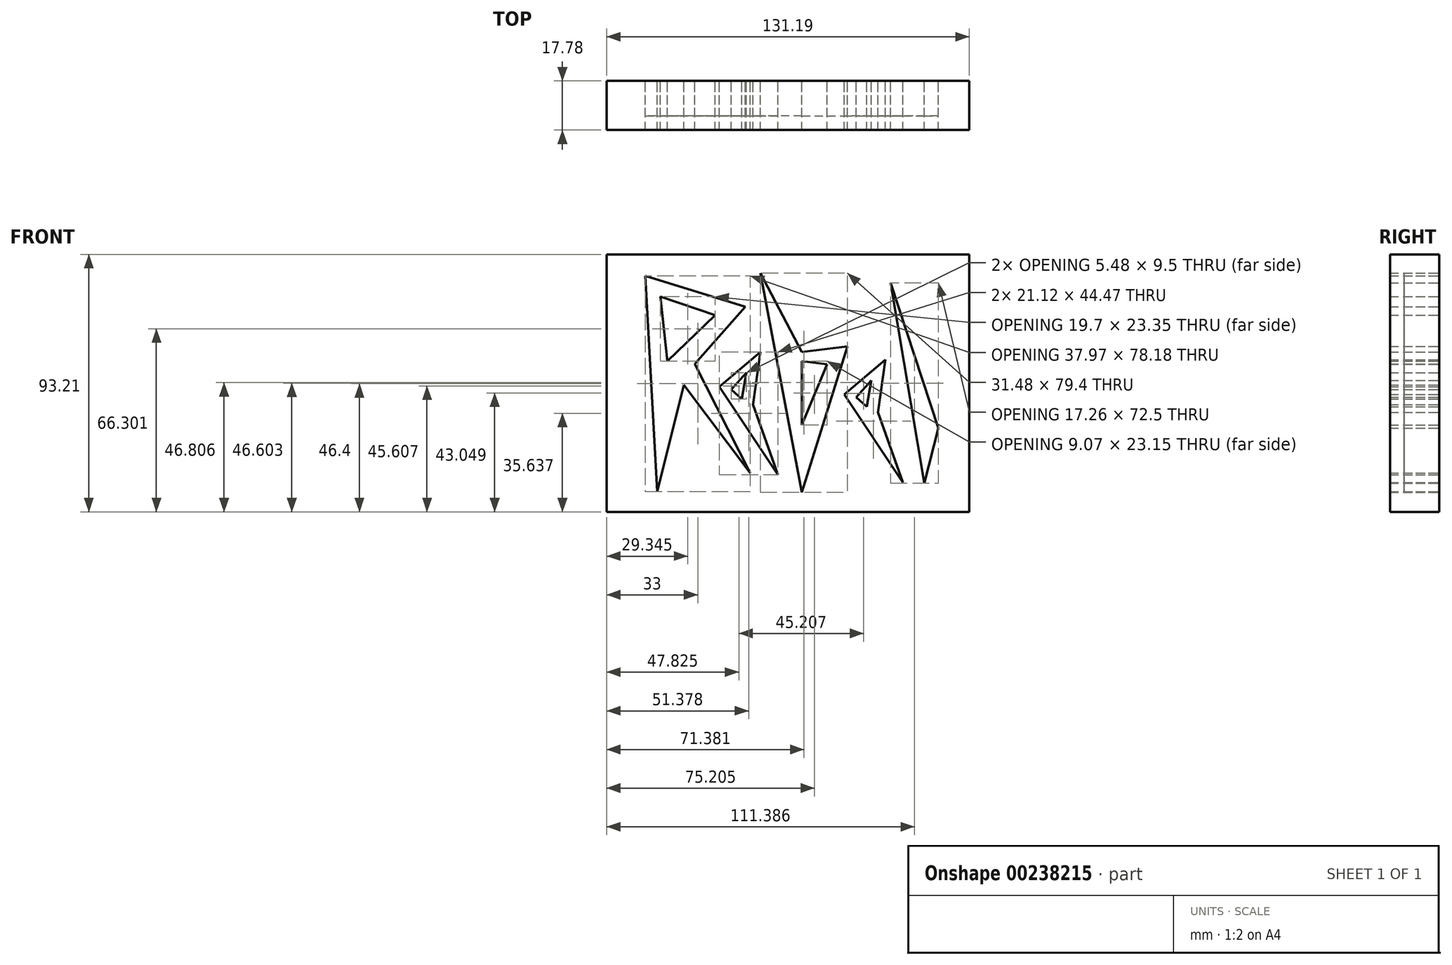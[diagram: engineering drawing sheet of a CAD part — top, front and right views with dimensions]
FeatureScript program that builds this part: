
annotation { "Feature Type Name" : "Feature", "Feature Type Description" : "" }
export const myFeature = defineFeature(function(context is Context, id is Id, definition is map)
    precondition{}
    {
        {
            var Q0;
            Q0=qCreatedBy(makeId("Front.planeOp"),FACE);
            var sketch = newSketch(context, id + "F0", { "sketchPlane" : qUnion([Q0])});
            skLineSegment(sketch, "E0", {"start": v(-56.66, 37.77) * mm, "end": v(-52.4, -40.41) * mm});
            skLineSegment(sketch, "E1", {"start": v(-52.4, -40.41) * mm, "end": v(-41.63, 2.64) * mm});
            skLineSegment(sketch, "E2", {"start": v(-41.63, 2.64) * mm, "end": v(-20.51, 26.6) * mm});
            skLineSegment(sketch, "E3", {"start": v(-20.51, 26.6) * mm, "end": v(-56.66, 37.77) * mm});
            skLineSegment(sketch, "E4", {"start": v(-51.17, 30.26) * mm, "end": v(-48.74, 6.9) * mm});
            skLineSegment(sketch, "E5", {"start": v(-48.74, 6.9) * mm, "end": v(-31.48, 23.56) * mm});
            skLineSegment(sketch, "E6", {"start": v(-31.48, 23.56) * mm, "end": v(-51.17, 30.26) * mm});
            skLineSegment(sketch, "E7", {"start": v(-38.8, 5.85) * mm, "end": v(-18.68, -33.7) * mm});
            skLineSegment(sketch, "E8", {"start": v(-18.68, -33.7) * mm, "end": v(-42.73, -1.76) * mm});
            skLineSegment(sketch, "E9", {"start": v(-15.03, 10.15) * mm, "end": v(-29.85, -2.44) * mm});
            skLineSegment(sketch, "E10", {"start": v(-29.85, -2.44) * mm, "end": v(-8.73, -34.32) * mm});
            skLineSegment(sketch, "E11", {"start": v(-8.73, -34.32) * mm, "end": v(-17.67, -8.94) * mm});
            skLineSegment(sketch, "E12", {"start": v(-17.67, -8.94) * mm, "end": v(-15.03, 10.15) * mm});
            skLineSegment(sketch, "E13", {"start": v(-20.1, 2.64) * mm, "end": v(-25.59, -3.45) * mm});
            skLineSegment(sketch, "E14", {"start": v(-25.59, -3.45) * mm, "end": v(-21.8, -6.87) * mm});
            skLineSegment(sketch, "E15", {"start": v(-21.8, -6.87) * mm, "end": v(-20.1, 2.64) * mm});
            skLineSegment(sketch, "E16", {"start": v(-15.03, 38.79) * mm, "end": v(0, -40.61) * mm});
            skLineSegment(sketch, "E17", {"start": v(0, -40.61) * mm, "end": v(16.45, 12.18) * mm});
            skLineSegment(sketch, "E18", {"start": v(16.45, 12.18) * mm, "end": v(0, 10.15) * mm});
            skLineSegment(sketch, "E19", {"start": v(0, 10.15) * mm, "end": v(-15.03, 38.79) * mm});
            skLineSegment(sketch, "E20", {"start": v(0, 6.9) * mm, "end": v(9.07, 5.65) * mm});
            skLineSegment(sketch, "E21", {"start": v(9.07, 5.65) * mm, "end": v(0, -16.25) * mm});
            skLineSegment(sketch, "E22", {"start": v(0, -16.25) * mm, "end": v(0, 6.9) * mm});
            skLineSegment(sketch, "E23", {"start": v(30.18, 7.4) * mm, "end": v(15.36, -5.2) * mm});
            skLineSegment(sketch, "E24", {"start": v(15.36, -5.2) * mm, "end": v(36.48, -37.08) * mm});
            skLineSegment(sketch, "E25", {"start": v(36.48, -37.08) * mm, "end": v(27.54, -11.7) * mm});
            skLineSegment(sketch, "E26", {"start": v(27.54, -11.7) * mm, "end": v(30.18, 7.4) * mm});
            skLineSegment(sketch, "E27", {"start": v(25.1, -0.12) * mm, "end": v(19.62, -6.21) * mm});
            skLineSegment(sketch, "E28", {"start": v(19.62, -6.21) * mm, "end": v(23.41, -9.63) * mm});
            skLineSegment(sketch, "E29", {"start": v(23.41, -9.63) * mm, "end": v(25.1, -0.12) * mm});
            skLineSegment(sketch, "E30", {"start": v(32.09, 35.13) * mm, "end": v(44.27, -37.37) * mm});
            skLineSegment(sketch, "E31", {"start": v(44.27, -37.37) * mm, "end": v(49.35, -17.46) * mm});
            skLineSegment(sketch, "E32", {"start": v(49.35, -17.46) * mm, "end": v(32.09, 35.13) * mm});
            skLineSegment(sketch, "E33.bottom", {"start": v(-70.67, 45.49) * mm, "end": v(60.52, 45.49) * mm});
            skLineSegment(sketch, "E33.top", {"start": v(-70.67, -47.72) * mm, "end": v(60.52, -47.72) * mm});
            skLineSegment(sketch, "E33.left", {"start": v(-70.67, 45.49) * mm, "end": v(-70.67, -47.72) * mm});
            skLineSegment(sketch, "E33.right", {"start": v(60.52, 45.49) * mm, "end": v(60.52, -47.72) * mm});
            skSolve(sketch);
        }
        {
            var Q0;
            {var subQ4=sQuery(id+"F0.wireOp",EDGE,"E0");Q0=makeQuery(id+"F0.imprint","IMPRINT",FACE,{"disambiguationData":[TD([[makeQuery(id+"F0.imprint","IMPRINT",EDGE,{"derivedFrom":subQ4}),-1.0]])]});}
            var Q1;
            Q1=makeQuery(id+"F0.imprint","IMPRINT",FACE,{"disambiguationData":[TD([[makeQuery(id+"F0.imprint","IMPRINT",EDGE,{"derivedFrom":sQuery(id+"F0.wireOp",EDGE,"E4")}),1.0]])]});
            var Q2;
            Q2=makeQuery(id+"F0.imprint","IMPRINT",FACE,{"disambiguationData":[TD([[makeQuery(id+"F0.imprint","IMPRINT",EDGE,{"derivedFrom":sQuery(id+"F0.wireOp",EDGE,"E13")}),1.0]])]});
            var Q3;
            Q3=makeQuery(id+"F0.imprint","IMPRINT",FACE,{"disambiguationData":[TD([[makeQuery(id+"F0.imprint","IMPRINT",EDGE,{"derivedFrom":sQuery(id+"F0.wireOp",EDGE,"E20")}),-1.0]])]});
            var Q4;
            Q4=makeQuery(id+"F0.imprint","IMPRINT",FACE,{"disambiguationData":[TD([[makeQuery(id+"F0.imprint","IMPRINT",EDGE,{"derivedFrom":sQuery(id+"F0.wireOp",EDGE,"E27")}),1.0]])]});
            extrude(context, id + "F1", {"entities" : qUnion([Q0, Q1, Q2, Q3, Q4]), "depth" : 17.78 * mm});
        }
        {
            var Q0;
            {var subQ5=sQuery(id+"F0.wireOp",EDGE,"E0");Q0=makeQuery(id+"F0.imprint","IMPRINT",FACE,{"disambiguationData":[TD([[makeQuery(id+"F0.imprint","IMPRINT",EDGE,{"derivedFrom":subQ5}),1.0]])]});}
            var Q1;
            {var subQ4=sQuery(id+"F0.wireOp",EDGE,"E7");Q1=makeQuery(id+"F0.imprint","IMPRINT",FACE,{"disambiguationData":[TD([[makeQuery(id+"F0.imprint","IMPRINT",EDGE,{"derivedFrom":subQ4}),-1.0]])]});}
            var Q2;
            Q2=makeQuery(id+"F0.imprint","IMPRINT",FACE,{"disambiguationData":[TD([[makeQuery(id+"F0.imprint","IMPRINT",EDGE,{"derivedFrom":sQuery(id+"F0.wireOp",EDGE,"E9")}),1.0]])]});
            var Q3;
            Q3=makeQuery(id+"F0.imprint","IMPRINT",FACE,{"disambiguationData":[TD([[makeQuery(id+"F0.imprint","IMPRINT",EDGE,{"derivedFrom":sQuery(id+"F0.wireOp",EDGE,"E16")}),1.0]])]});
            var Q4;
            Q4=makeQuery(id+"F0.imprint","IMPRINT",FACE,{"disambiguationData":[TD([[makeQuery(id+"F0.imprint","IMPRINT",EDGE,{"derivedFrom":sQuery(id+"F0.wireOp",EDGE,"E23")}),1.0]])]});
            var Q5;
            Q5=makeQuery(id+"F0.imprint","IMPRINT",FACE,{"disambiguationData":[TD([[makeQuery(id+"F0.imprint","IMPRINT",EDGE,{"derivedFrom":sQuery(id+"F0.wireOp",EDGE,"E30")}),1.0]])]});
            extrude(context, id + "F2", {"entities" : qUnion([Q0, Q1, Q2, Q3, Q4, Q5]), "depth" : 12.7 * mm});
        }
    });
